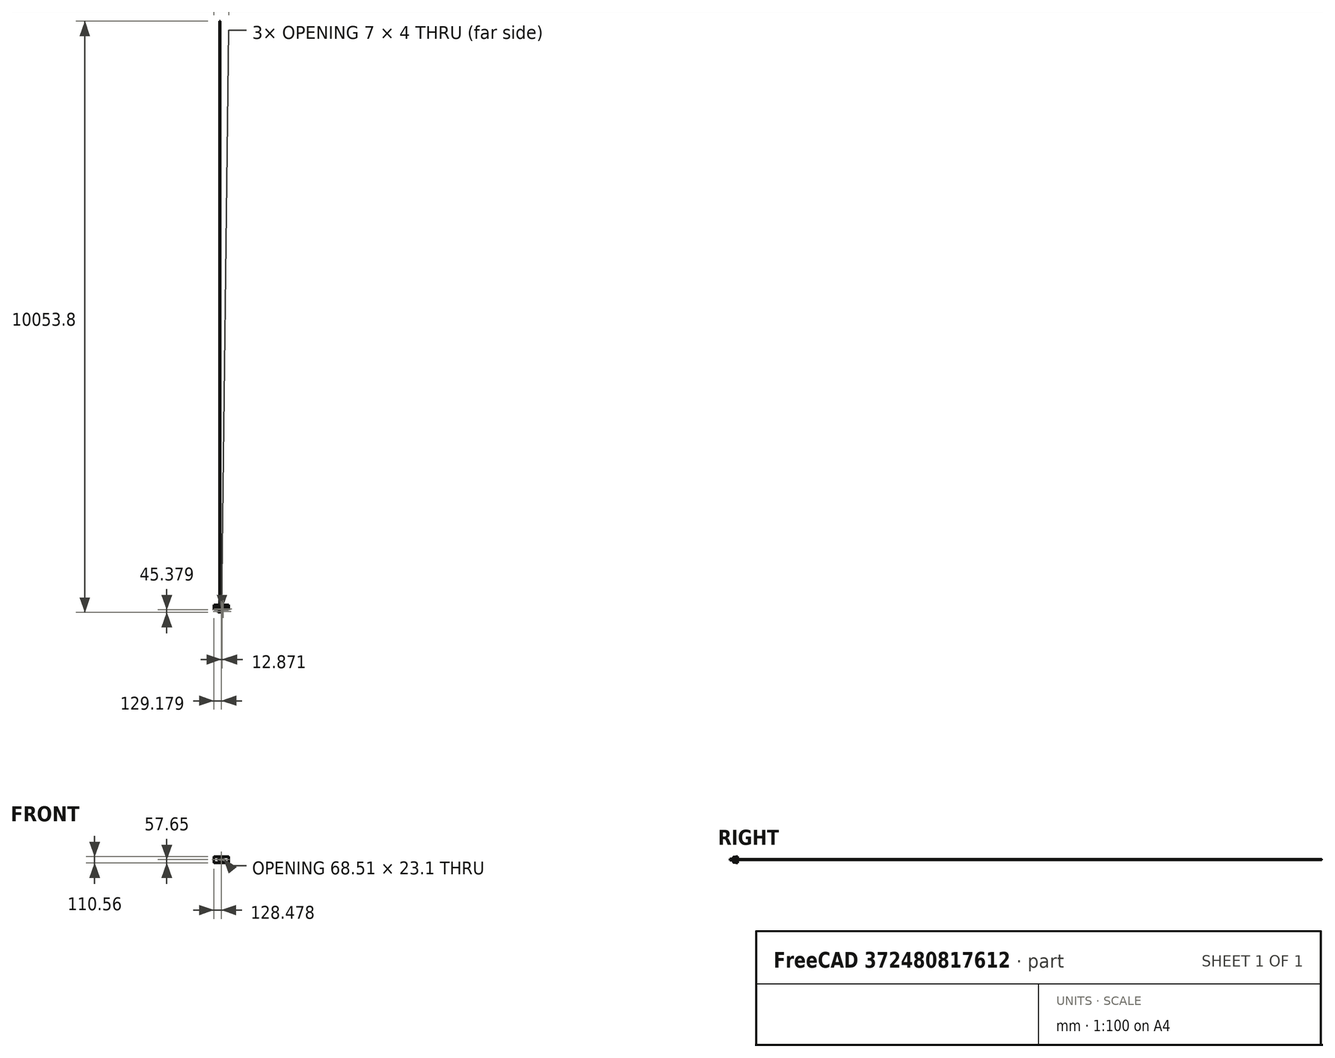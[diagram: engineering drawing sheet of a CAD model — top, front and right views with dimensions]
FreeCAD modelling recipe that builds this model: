
FCSTD DOCUMENT  (FreeCAD 0.16R5480 (Git))
Label: flexystruder_body_holderV0.1
License: CreativeCommons Attribution-ShareAlike
LicenseURL: http://creativecommons.org/licenses/by-sa/4.0/
objects: Sketcher::SketchObject×7, PartDesign::Pocket×5, Part::Feature×4, PartDesign::Pad×2, Mesh::Feature×1, PartDesign::Fillet×1, Part::Cut×1
note: 27 computed .brp shape members not serialized (recipe doc carries the construction recipe); baked Part::Feature solids carry a one-line shape summary decoded from their .brp

FEATURE [Mesh::Feature] flexystruder_body_hex_v2_0  label="flexystruder_body_hex_v2.0"
FEATURE [Part::Feature] flexystruder_body_hex_v2_0001
  shape: bbox 97.06 x 64.55 x 27.5 mm, 7934 faces, 0 solids (baked)
FEATURE [Part::Feature] flexystruder_body_hex_v2_0001001  label="flexystruder_body_hex_v2_0002"
  shape: bbox 97.06 x 64.55 x 27.5 mm, 4378 faces, 0 solids (baked)
FEATURE [Part::Feature] flexystruder_body_hex_v2_0001001_solid  label="flexystruder_body_hex_v2_0002 (Solid)"
  shape: bbox 97.06 x 64.55 x 27.5 mm, 4378 faces (baked)
FEATURE [Sketcher::SketchObject] Sketch
  Placement = pos=(0,0,0) rot=(0.57735,0.57735,0.57735;2.0944rad)
  sketch-geometry (4):
    g0: LineSegment StartX=53.7731 StartY=-40 StartZ=0 EndX=92.5361 EndY=-40 EndZ=0
    g1: LineSegment StartX=92.5361 StartY=-40 StartZ=0 EndX=92.5361 EndY=60 EndZ=0
    g2: LineSegment StartX=92.5361 StartY=60 StartZ=0 EndX=53.7731 EndY=60 EndZ=0
    g3: LineSegment StartX=53.7731 StartY=60 StartZ=0 EndX=53.7731 EndY=-40 EndZ=0
  constraints (10):
    c: Coincident(g0,g1)
    c: Coincident(g1,g2)
    c: Coincident(g2,g3)
    c: Coincident(g3,g0)
    c: Horizontal(g0)
    c: Horizontal(g2)
    c: Vertical(g1)
    c: Vertical(g3)
    c: DistanceY(g1) = 100
    c: DistanceY(g-1,g0) = -40
FEATURE [PartDesign::Pad] Pad
  Length = 150
  Length2 = 100
  Placement = pos=(0,0,0) rot=(0.57735,0.57735,0.57735;2.0944rad)
  Sketch = -> Sketch
  Type = 4
FEATURE [PartDesign::Fillet] Fillet
  Base = -> Pad [Edge8,Edge1,Edge12,Edge11,Edge10,Edge4,Edge9,Edge3]
  Placement = pos=(0,0,0) rot=(0.57735,0.57735,0.57735;2.0944rad)
  Radius = 10
FEATURE [Sketcher::SketchObject] Sketch001
  Placement = pos=(0,0,0) rot=(1,0,0;3.14159rad)
  Support = -> flexystruder_body_hex_v2_0001001_solid [Face1922]
  sketch-geometry (4):
    g0: ArcOfCircle CenterX=52 CenterY=-58.243 CenterZ=0 NormalX=0 NormalY=0 NormalZ=1 Radius=4.06074 StartAngle=1.5708 EndAngle=4.71239
    g1: ArcOfCircle CenterX=56.5198 CenterY=-58.243 CenterZ=0 NormalX=0 NormalY=0 NormalZ=1 Radius=4.06074 StartAngle=4.71239 EndAngle=7.85398
    g2: LineSegment StartX=52 StartY=-62.3037 StartZ=0 EndX=56.5198 EndY=-62.3037 EndZ=0
    g3: LineSegment StartX=52 StartY=-54.1822 StartZ=0 EndX=56.5198 EndY=-54.1822 EndZ=0
  constraints (6):
    c: Tangent(g0,g3) = 1.5708
    c: Tangent(g0,g2) = -1.5708
    c: Tangent(g2,g1) = -1.5708
    c: Tangent(g3,g1) = 1.5708
    c: Horizontal(g2)
    c: Equal(g0,g1)
FEATURE [PartDesign::Pad] Pad001
  Length = 9.5
  Length2 = 100
  Reversed = true
  Sketch = -> Sketch001
  Type = 0
FEATURE [Part::Cut] Cut
  Base = -> Fillet
  Tool = -> Pad001
FEATURE [Sketcher::SketchObject] Sketch002
  Placement = pos=(0,53.7731,0) rot=(1,0,0;1.5708rad)
  Support = -> Cut [Face403]
  sketch-geometry (1):
    g0: Circle CenterX=0.482362 CenterY=14 CenterZ=0 NormalX=0 NormalY=0 NormalZ=1 Radius=5
  constraints (1):
    c: Radius(g0) = 5
FEATURE [PartDesign::Pocket] Pocket
  Length = 5
  Sketch = -> Sketch002
  Type = 1
FEATURE [Part::Feature] Pocket001
  shape: bbox 250 x 78.23 x 100 mm, 1139 faces (baked)
FEATURE [Sketcher::SketchObject] Sketch003
  ExternalGeometry = -> [Pocket001]
  Placement = pos=(0,53.7731,0) rot=(1,0,0;1.5708rad)
  Support = -> Pocket001 [Face62]
  sketch-geometry (4):
    g0: LineSegment StartX=44.0071 StartY=0 StartZ=0 EndX=51.0275 EndY=0 EndZ=0
    g1: LineSegment StartX=51.0275 StartY=0 StartZ=0 EndX=51.0275 EndY=1.89901 EndZ=0
    g2: LineSegment StartX=51.0275 StartY=1.89901 StartZ=0 EndX=44.0071 EndY=1.89901 EndZ=0
    g3: LineSegment StartX=44.0071 StartY=1.89901 StartZ=0 EndX=44.0071 EndY=0 EndZ=0
  constraints (9):
    c: Coincident(g0,g1)
    c: Coincident(g1,g2)
    c: Coincident(g2,g3)
    c: Coincident(g3,g0)
    c: Horizontal(g0)
    c: Horizontal(g2)
    c: Vertical(g1)
    c: Vertical(g3)
    c: Coincident(g0,g-4)
FEATURE [PartDesign::Pocket] Pocket002
  Length = 5
  Sketch = -> Sketch003
  Type = 0
FEATURE [Sketcher::SketchObject] Sketch004
  ExternalGeometry = -> [Pocket002]
  Placement = pos=(0,53.7731,0) rot=(1,0,0;1.5708rad)
  Support = -> Pocket002 [Face6]
  sketch-geometry (4):
    g0: LineSegment StartX=59.4175 StartY=0 StartZ=0 EndX=62 EndY=0 EndZ=0
    g1: LineSegment StartX=62 StartY=0 StartZ=0 EndX=62 EndY=9.5 EndZ=0
    g2: LineSegment StartX=62 StartY=9.5 StartZ=0 EndX=59.4175 EndY=9.5 EndZ=0
    g3: LineSegment StartX=59.4175 StartY=9.5 StartZ=0 EndX=59.4175 EndY=0 EndZ=0
  constraints (10):
    c: Coincident(g0,g1)
    c: Coincident(g1,g2)
    c: Coincident(g2,g3)
    c: Coincident(g3,g0)
    c: Horizontal(g0)
    c: Horizontal(g2)
    c: Vertical(g1)
    c: Vertical(g3)
    c: Coincident(g0,g-4)
    c: PointOnObject(g2,g-3)
FEATURE [PartDesign::Pocket] Pocket003
  Length = 6
  Sketch = -> Sketch004
  Type = 0
FEATURE [Sketcher::SketchObject] Sketch005
  Placement = pos=(0,53.7731,0) rot=(1,0,0;1.5708rad)
  Support = -> Pocket003 [Face6]
  sketch-geometry (4):
    g0: LineSegment StartX=-9 StartY=23.4478 StartZ=0 EndX=62.6602 EndY=23.4478 EndZ=0
    g1: LineSegment StartX=62.6602 StartY=23.4478 StartZ=0 EndX=62.6602 EndY=-0.539133 EndZ=0
    g2: LineSegment StartX=62.6602 StartY=-0.539133 StartZ=0 EndX=-9 EndY=-0.539133 EndZ=0
    g3: LineSegment StartX=-9 StartY=-0.539133 StartZ=0 EndX=-9 EndY=23.4478 EndZ=0
  constraints (8):
    c: Coincident(g0,g1)
    c: Coincident(g1,g2)
    c: Coincident(g2,g3)
    c: Coincident(g3,g0)
    c: Horizontal(g0)
    c: Horizontal(g2)
    c: Vertical(g1)
    c: Vertical(g3)
FEATURE [PartDesign::Pocket] Pocket004
  Length = 1
  Sketch = -> Sketch005
  Type = 0
FEATURE [Sketcher::SketchObject] Sketch006
  Placement = pos=(0,132,0) rot=(0,0.707107,0.707107;3.14159rad)
  Support = -> Pocket004 [Face351]
  sketch-geometry (4):
    g0: LineSegment StartX=102.553 StartY=64.4599 StartZ=0 EndX=-151.782 EndY=64.4599 EndZ=0
    g1: LineSegment StartX=-151.782 StartY=64.4599 StartZ=0 EndX=-151.782 EndY=-46.0981 EndZ=0
    g2: LineSegment StartX=-151.782 StartY=-46.0981 StartZ=0 EndX=102.553 EndY=-46.0981 EndZ=0
    g3: LineSegment StartX=102.553 StartY=-46.0981 StartZ=0 EndX=102.553 EndY=64.4599 EndZ=0
  constraints (8):
    c: Coincident(g0,g1)
    c: Coincident(g1,g2)
    c: Coincident(g2,g3)
    c: Coincident(g3,g0)
    c: Horizontal(g0)
    c: Horizontal(g2)
    c: Vertical(g1)
    c: Vertical(g3)
FEATURE [PartDesign::Pocket] Pocket005
  Length = 35
  Sketch = -> Sketch006
  Type = 0
